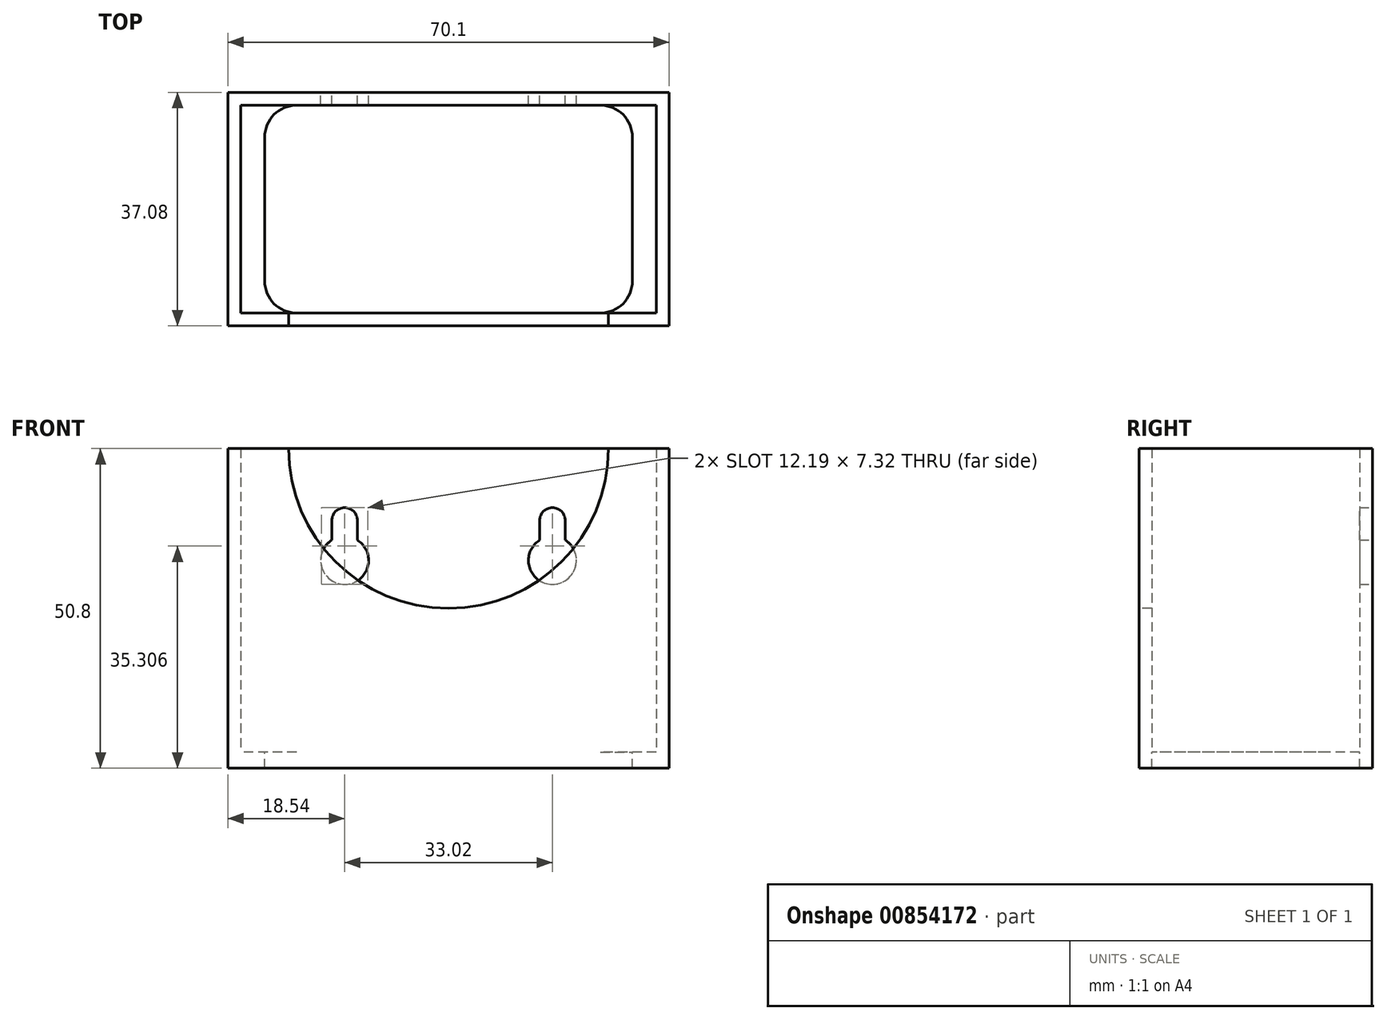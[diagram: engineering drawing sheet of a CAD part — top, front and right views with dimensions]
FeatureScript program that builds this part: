
annotation { "Feature Type Name" : "Feature", "Feature Type Description" : "" }
export const myFeature = defineFeature(function(context is Context, id is Id, definition is map)
    precondition{}
    {
        {
            var Q0;
            Q0=qCreatedBy(makeId("Top.planeOp"),FACE);
            var sketch = newSketch(context, id + "F0", { "sketchPlane" : qUnion([Q0])});
            skLineSegment(sketch, "E0", {"start": v(0, 0) * mm, "end": v(66.04, 0) * mm});
            skLineSegment(sketch, "E1", {"start": v(66.04, 0) * mm, "end": v(66.04, 33.02) * mm});
            skLineSegment(sketch, "E2", {"start": v(66.04, 33.02) * mm, "end": v(0, 33.02) * mm});
            skLineSegment(sketch, "E3", {"start": v(0, 33.02) * mm, "end": v(0, 0) * mm});
            skLineSegment(sketch, "E4", {"start": v(-2.03, -2.03) * mm, "end": v(68.07, -2.03) * mm});
            skLineSegment(sketch, "E5", {"start": v(68.07, -2.03) * mm, "end": v(68.07, 35.05) * mm});
            skLineSegment(sketch, "E6", {"start": v(68.07, 35.05) * mm, "end": v(-2.03, 35.05) * mm});
            skLineSegment(sketch, "E7", {"start": v(-2.03, 35.05) * mm, "end": v(-2.03, -2.03) * mm});
            skSolve(sketch);
        }
        {
            var Q0;
            Q0=makeQuery(id+"F0.imprint","IMPRINT",FACE,{"disambiguationData":[TD([[makeQuery(id+"F0.imprint","IMPRINT",EDGE,{"derivedFrom":sQuery(id+"F0.wireOp",EDGE,"E0")}),-1.0]])]});
            extrude(context, id + "F1", {"entities" : qUnion([Q0]), "depth" : 50.8 * mm, "offsetDistance" : 25.4 * mm});
        }
        {
            var Q0;
            Q0=makeQuery(id+"F0.imprint","IMPRINT",FACE,{"disambiguationData":[TD([[makeQuery(id+"F0.imprint","IMPRINT",EDGE,{"derivedFrom":sQuery(id+"F0.wireOp",EDGE,"E0")}),1.0]])]});
            extrude(context, id + "F2", {"entities" : qUnion([Q0]), "operationType" : NewBodyOperationType.ADD, "depth" : 2.54 * mm, "offsetDistance" : 25.4 * mm});
        }
        {
            var Q0;
            Q0=makeQuery(id+"F2.opExtrude","CAP_FACE",FACE,{"disambiguationData":[OSD([sQuery(id+"F0.wireOp",EDGE,"E0"),sQuery(id+"F0.wireOp",EDGE,"E1"),sQuery(id+"F0.wireOp",EDGE,"E2"),sQuery(id+"F0.wireOp",EDGE,"E3")])],"isStart":false});
            var sketch = newSketch(context, id + "F3", { "sketchPlane" : qUnion([Q0])});
            skLineSegment(sketch, "E8", {"start": v(3.81, 33.02) * mm, "end": v(3.81, 0) * mm});
            skLineSegment(sketch, "E9", {"start": v(3.81, 0) * mm, "end": v(62.23, 0) * mm});
            skLineSegment(sketch, "E10", {"start": v(62.23, 0) * mm, "end": v(62.23, 33.02) * mm});
            skLineSegment(sketch, "E11", {"start": v(62.23, 33.02) * mm, "end": v(3.81, 33.02) * mm});
            skSolve(sketch);
        }
        {
            var Q0;
            Q0=makeQuery(id+"F3.imprint","IMPRINT",FACE,{"disambiguationData":[TD([[makeQuery(id+"F3.imprint","IMPRINT",EDGE,{"derivedFrom":sQuery(id+"F3.wireOp",EDGE,"E8")}),1.0]])]});
            extrude(context, id + "F4", {"entities" : qUnion([Q0]), "operationType" : NewBodyOperationType.REMOVE, "oppositeDirection" : true, "depth" : 25.4 * mm, "offsetDistance" : 25.4 * mm});
        }
        {
            var Q0;
            Q0=makeQuery(id+"F1.opExtrude","SWEPT_FACE",FACE,{"disambiguationData":[OSD([sQuery(id+"F0.wireOp",EDGE,"E4")])]});
            var sketch = newSketch(context, id + "F5", { "sketchPlane" : qUnion([Q0])});
            skArc(sketch, "E12", {"start": v(7.62, 50.8) * mm, "mid": v(33.02, 25.4) * mm, "end": v(58.42, 50.8) * mm});
            skSolve(sketch);
        }
        {
            var Q0;
            {var subQ0=sQuery(id+"F5.wireOp",EDGE,"E12");Q0=makeQuery(id+"F5.imprint","IMPRINT",FACE,{"disambiguationData":[TD([[makeQuery(id+"F5.imprint","IMPRINT",EDGE,{"derivedFrom":subQ0}),1.0]])]});}
            extrude(context, id + "F6", {"entities" : qUnion([Q0]), "operationType" : NewBodyOperationType.REMOVE, "oppositeDirection" : true, "depth" : 25.4 * mm, "offsetDistance" : 25.4 * mm});
        }
        {
            var Q0;
            Q0=makeQuery(id+"F1.opExtrude","SWEPT_FACE",FACE,{"disambiguationData":[OSD([sQuery(id+"F0.wireOp",EDGE,"E6")])]});
            var sketch = newSketch(context, id + "F7", { "sketchPlane" : qUnion([Q0])});
            skLineSegment(sketch, "E13", {"start": v(-33.02, 61.29) * mm, "end": v(-33.02, -15.49) * mm, "construction": true});
            skPoint(sketch, "E13.startSnap0", {"position": v(-33.02, 50.8) * mm});
            skLineSegment(sketch, "E14", {"start": v(14.16, 25.4) * mm, "end": v(-84.82, 25.4) * mm, "construction": true});
            skPoint(sketch, "E14.startSnap0", {"position": v(2.03, 25.4) * mm});
            skCircle(sketch, "E15", {"center": v(-16.51, 33.02) * mm, "radius": 3.81 * mm});
            skCircle(sketch, "E16", {"center": v(-49.53, 33.02) * mm, "radius": 3.81 * mm});
            skLineSegment(sketch, "E17", {"start": v(-47.5, 33.02) * mm, "end": v(-47.5, 39.37) * mm, "construction": true});
            skLineSegment(sketch, "E18", {"start": v(-47.5, 39.37) * mm, "end": v(-51.56, 39.37) * mm, "construction": true});
            skLineSegment(sketch, "E19", {"start": v(-51.56, 39.37) * mm, "end": v(-51.56, 33.02) * mm, "construction": true});
            skArc(sketch, "E20", {"start": v(-47.5, 39.37) * mm, "mid": v(-49.53, 41.4) * mm, "end": v(-51.56, 39.37) * mm});
            skLineSegment(sketch, "E21", {"start": v(-51.56, 39.37) * mm, "end": v(-51.56, 36.24) * mm});
            skLineSegment(sketch, "E22", {"start": v(-47.5, 39.37) * mm, "end": v(-47.5, 36.24) * mm});
            skLineSegment(sketch, "E23", {"start": v(-16.51, 33.02) * mm, "end": v(-16.51, 43.77) * mm, "construction": true});
            skLineSegment(sketch, "E24", {"start": v(-18.54, 39.37) * mm, "end": v(-18.54, 36.24) * mm});
            skArc(sketch, "E25", {"start": v(-18.54, 39.37) * mm, "mid": v(-16.51, 41.4) * mm, "end": v(-14.48, 39.37) * mm});
            skLineSegment(sketch, "E26", {"start": v(-14.48, 39.37) * mm, "end": v(-14.48, 36.24) * mm});
            skSolve(sketch);
        }
        {
            var Q0;
            {var subQ0=sQuery(id+"F7.wireOp",EDGE,"E16");var subQ1=makeQuery(id+"F7.imprint","INTERSECT",VERTEX,{"derivedFrom":[subQ0,sQuery(id+"F7.wireOp",EDGE,"E21")]});Q0=makeQuery(id+"F7.imprint","IMPRINT",FACE,{"disambiguationData":[TD([[makeQuery(id+"F7.imprint","IMPRINT",EDGE,{"disambiguationData":[TD([[subQ1,1.0]])],"derivedFrom":subQ0}),1.0]])]});}
            var Q1;
            Q1=makeQuery(id+"F7.imprint","IMPRINT",FACE,{"disambiguationData":[TD([[makeQuery(id+"F7.imprint","IMPRINT",EDGE,{"derivedFrom":sQuery(id+"F7.wireOp",EDGE,"E20")}),1.0]])]});
            var Q2;
            {var subQ0=sQuery(id+"F7.wireOp",EDGE,"E24");Q2=makeQuery(id+"F7.imprint","IMPRINT",FACE,{"disambiguationData":[TD([[makeQuery(id+"F7.imprint","IMPRINT",EDGE,{"derivedFrom":subQ0}),1.0]])]});}
            var Q3;
            {var subQ0=sQuery(id+"F7.wireOp",EDGE,"E15");var subQ1=makeQuery(id+"F7.imprint","INTERSECT",VERTEX,{"derivedFrom":[subQ0,sQuery(id+"F7.wireOp",EDGE,"E24")]});Q3=makeQuery(id+"F7.imprint","IMPRINT",FACE,{"disambiguationData":[TD([[makeQuery(id+"F7.imprint","IMPRINT",EDGE,{"disambiguationData":[TD([[subQ1,1.0]])],"derivedFrom":subQ0}),1.0]])]});}
            extrude(context, id + "F8", {"entities" : qUnion([Q0, Q1, Q2, Q3]), "operationType" : NewBodyOperationType.REMOVE, "oppositeDirection" : true, "depth" : 25.4 * mm, "offsetDistance" : 25.4 * mm});
        }
        {
            var Q0;
            {var subQ0=sQuery(id+"F5.wireOp",EDGE,"E12");var subQ1=sQuery(id+"F0.wireOp",EDGE,"E4");Q0=makeQuery(id+"F6.boolean.opBoolean","COPY",EDGE,{"derivedFrom":makeQuery(id+"F6.opExtrude","SWEPT_EDGE",EDGE,{"disambiguationData":[OSD([subQ1,subQ0]),TDD([makeQuery(id+"F5.imprint","INTERSECT",VERTEX,{"disambiguationData":[OD(1.0)],"derivedFrom":[makeQuery(id+"F1.opExtrude","CAP_EDGE",EDGE,{"disambiguationData":[OSD([subQ1])],"isStart":false}),subQ0]})])]})});}
            var Q1;
            {var subQ0=sQuery(id+"F5.wireOp",EDGE,"E12");var subQ1=sQuery(id+"F0.wireOp",EDGE,"E4");Q1=makeQuery(id+"F6.boolean.opBoolean","COPY",EDGE,{"derivedFrom":makeQuery(id+"F6.opExtrude","SWEPT_EDGE",EDGE,{"disambiguationData":[OSD([subQ1,subQ0]),TDD([makeQuery(id+"F5.imprint","INTERSECT",VERTEX,{"disambiguationData":[OD(0.0)],"derivedFrom":[makeQuery(id+"F1.opExtrude","CAP_EDGE",EDGE,{"disambiguationData":[OSD([subQ1])],"isStart":false}),subQ0]})])]})});}
            var Q2;
            Q2=makeQuery(id+"F4.boolean.opBoolean","COPY",EDGE,{"derivedFrom":makeQuery(id+"F4.opExtrude","SWEPT_EDGE",EDGE,{"disambiguationData":[OSD([sQuery(id+"F0.wireOp",EDGE,"E0"),sQuery(id+"F3.wireOp",EDGE,"E9"),sQuery(id+"F3.wireOp",EDGE,"E10")])]})});
            var Q3;
            Q3=makeQuery(id+"F4.boolean.opBoolean","COPY",EDGE,{"derivedFrom":makeQuery(id+"F4.opExtrude","SWEPT_EDGE",EDGE,{"disambiguationData":[OSD([sQuery(id+"F0.wireOp",EDGE,"E2"),sQuery(id+"F3.wireOp",EDGE,"E10"),sQuery(id+"F3.wireOp",EDGE,"E11")])]})});
            var Q4;
            Q4=makeQuery(id+"F4.boolean.opBoolean","COPY",EDGE,{"derivedFrom":makeQuery(id+"F4.opExtrude","SWEPT_EDGE",EDGE,{"disambiguationData":[OSD([sQuery(id+"F0.wireOp",EDGE,"E2"),sQuery(id+"F3.wireOp",EDGE,"E8"),sQuery(id+"F3.wireOp",EDGE,"E11")])]})});
            var Q5;
            Q5=makeQuery(id+"F4.boolean.opBoolean","COPY",EDGE,{"derivedFrom":makeQuery(id+"F4.opExtrude","SWEPT_EDGE",EDGE,{"disambiguationData":[OSD([sQuery(id+"F0.wireOp",EDGE,"E0"),sQuery(id+"F3.wireOp",EDGE,"E8"),sQuery(id+"F3.wireOp",EDGE,"E9")])]})});
            fillet(context, id + "F9", {"entities" : qUnion([Q0, Q1, Q2, Q3, Q4, Q5]), "radius" : 5.08 * mm, "tangentPropagation" : true, "allowEdgeOverflow" : false});
        }
    });
